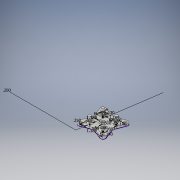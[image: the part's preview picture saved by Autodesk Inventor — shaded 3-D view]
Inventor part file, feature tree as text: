
AUTODESK INVENTOR PART (.ipt)
format: ipt  version: 2017 (Build 210142000, 142)  size: 217,600 bytes
history: native  units: in
note: dims shown in document units (in); Inventor stores cm internally (conversion verified against a paired STEP export)
features: extrude x3, fillet x2, sketch x1
ambient origin geometry x8: Origin, YZ Plane, XZ Plane, XY Plane, X Axis, Y Axis, Z Axis, Center Point
bodies: Solid1 (feature_tree)
feature tree (6):
  sketch  "Sketch1"  dims[d0=0.6969in d1=0.7047in d2=0.1398in d3=0.1398in d4=0.1398in d5=0.1398in d9=0.3937in d10=0.0in d11=0.2in d12=0.2in d13=0.2in d14=0.2in d15=0.2362in d16=0.0in d31=0.1299in d32=0.7874in d34=1.189in d35=0.7874in d37=1.189in d68=0.25in d69=0.7874in d71=1.189in d72=0.7874in d74=1.189in d78=0.5in d79=0.5in d81=0.5in d82=0.0984in d83=0.0in d84=0.3937in d85=0.0787in]
  extrude  "Extrusion2"  Depth=0.0787in
  extrude  "Extrusion3"  Depth=0.0787in
  extrude  "Extrusion6"  Depth=0.0787in
  fillet  "Fillet2"  Radius=0.1398in
  fillet  "Fillet3"  Radius=0.1398in
